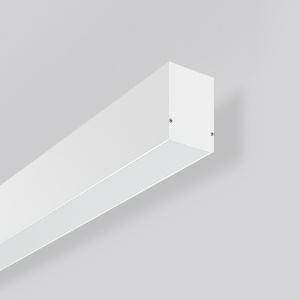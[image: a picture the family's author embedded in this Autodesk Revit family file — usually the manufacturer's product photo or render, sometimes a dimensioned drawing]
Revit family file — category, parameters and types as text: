
# Revit family: less_is_more_50_312607_002_1_76_d5f6
name_source: partatom
category: Lighting Fixtures
units: mm (PartAtom-declared; Revit-internal decimal feet)

## family parameters
Cut with Voids When Loaded = No
Host = Face
Light Source = No
Part Type = Normal
Room Calculation Point = No
Round Connector Dimension = Use Diameter
Shared = No

## types (1)
- LESS IS MORE 50 (1 x LED Modul 840, 1500 lm, 4000)
    Apparent Load = 13 VA
    CIE Flux Codes = 48 80 96 100 100
    Color Rendering = 80
    Color Temperature = 4000
    Default Elevation = 1800 mm
    Description = Series: LESS IS MORE 50
Linear wall luminaires. Housing: extruded aluminium profile, powder-coated. End cap aluminium powder-coated. Diffuser made of non-yellowing plastic (PMMA), opal. Direct light emission. Suitable for Wall (surface). LED unit with integrated converter interchangeable and removable. Suitable for through-wiring. With sensors or as a safety luminaire on request. 
Colour: traffic white, matt (RAL 9016)
Length: 1127 mm
Width: 67 mm
Height: 75 mm
Lamp: LED
Socket: without socket
Colour temperature: 4000K
Colour rendering index (CRI): 80
System power: 13 W
Rated luminous flux: 1500 lm
Luminous efficiency: 115 lm/W
Control gear: Converter, dimmable, DALI
Protection class: I
Type of protection: IP 20
    Height = 75 mm
    Lamp = 1 x LED Modul 840
    Lamp Light Flux = 1500 lm
    Lamp count = 1
    Length = 1127 mm
    Lifetime = 50000 h
    Luminous efficacy = 115 lm/W
    Manufacturer = RZB
    ModVariant = No
    Model = 312607.002.1.76
    Mounting Place = Wall
    Mounting Type = Surface mounted
    Number of Poles = 1
    OnlyDefault = Yes
    Power Factor = 1
    Product Name = LESS IS MORE 50
    Product group = Surface mounted LED linear luminaires
    ProductGroupID = 2007
    Protection Class = Protection class I
    Protection Degree = IP 20
    RLX_Detail_Level = 1
    RLX_Emergency_Light_Flux = 0 lm
    RLX_Emergency_Type = 0
    RLX_Emergency_Type_DB = No
    RlxData = <blob elided: 35197 chars, md5=3bb98d8f>
    Socket = socket
    Standby Power = 0 W
    System Light Flux = 1500 lm
    System Power = 13 W
    Type Comments = Product without accessories
    Type Image = 312606.002.jpg
    URL = http://relux.com
    VarID = ---
    Voltage = 0 V
    Weight = 0.00 kg
    Width = 67 mm

## geometry (parser evidence)
native form markers: Blend x4, Sweep x11
no freeform markers — native parametric forms only
